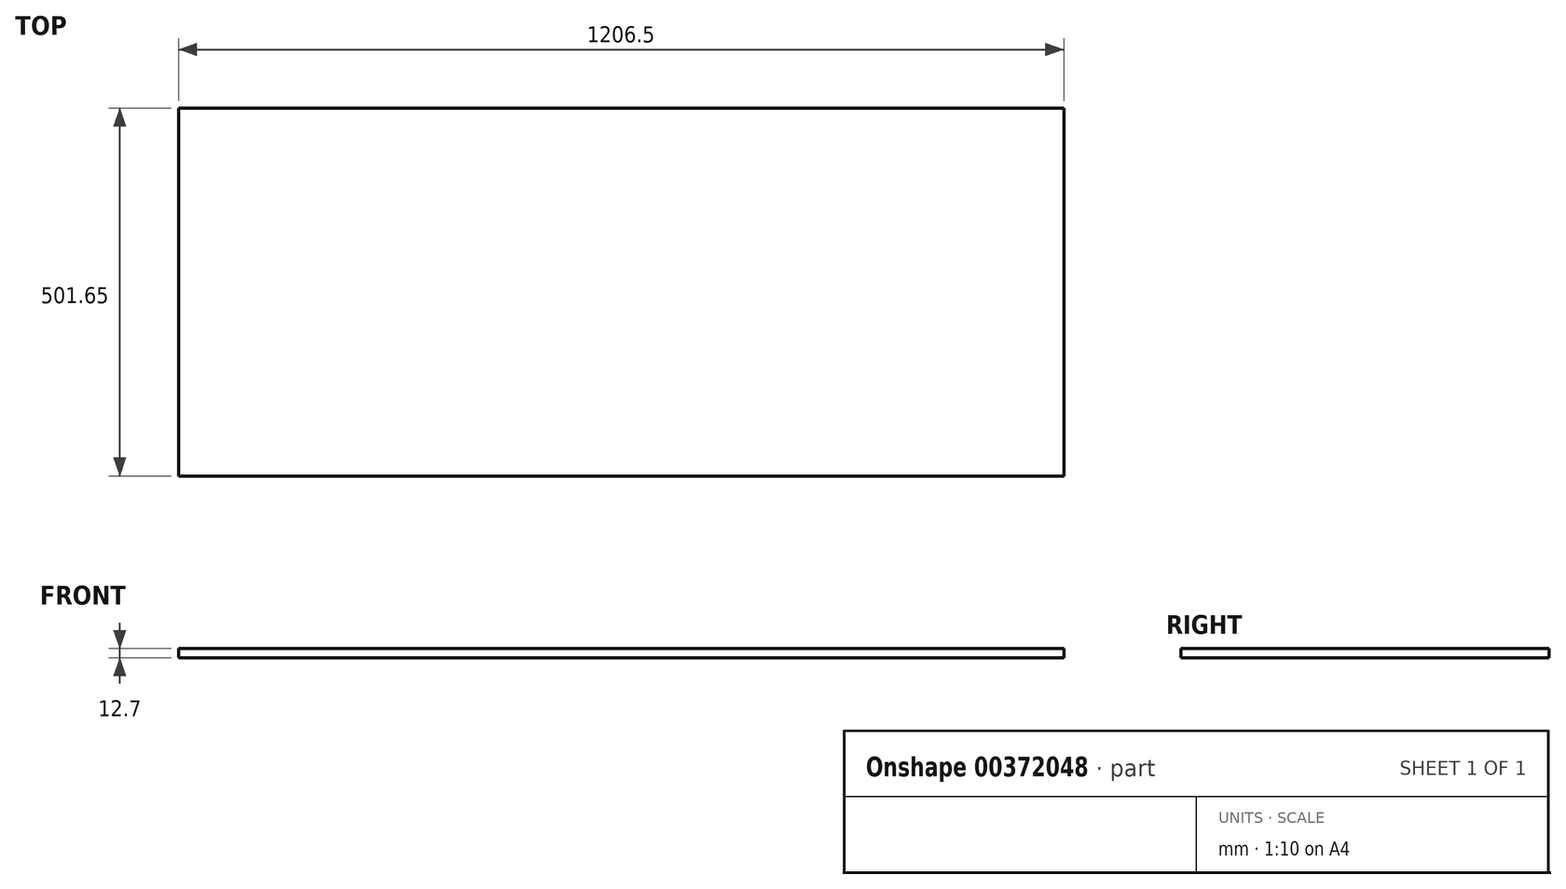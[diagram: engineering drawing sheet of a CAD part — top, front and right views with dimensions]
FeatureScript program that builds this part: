
annotation { "Feature Type Name" : "Feature", "Feature Type Description" : "" }
export const myFeature = defineFeature(function(context is Context, id is Id, definition is map)
    precondition{}
    {
        {
            var Q0;
            Q0=qCreatedBy(makeId("Top.planeOp"),FACE);
            var sketch = newSketch(context, id + "F0", { "sketchPlane" : qUnion([Q0])});
            skLineSegment(sketch, "E0.bottom", {"start": v(-521.92, 0) * mm, "end": v(684.58, 0) * mm});
            skLineSegment(sketch, "E0.top", {"start": v(-521.92, 501.65) * mm, "end": v(684.58, 501.65) * mm});
            skLineSegment(sketch, "E0.left", {"start": v(-521.92, 0) * mm, "end": v(-521.92, 501.65) * mm});
            skLineSegment(sketch, "E0.right", {"start": v(684.58, 0) * mm, "end": v(684.58, 501.65) * mm});
            skSolve(sketch);
        }
        {
            var Q0;
            Q0 = qSketchRegion(id + "F0", true);
            extrude(context, id + "F1", {"entities" : qUnion([Q0]), "depth" : 12.7 * mm});
        }
    });
